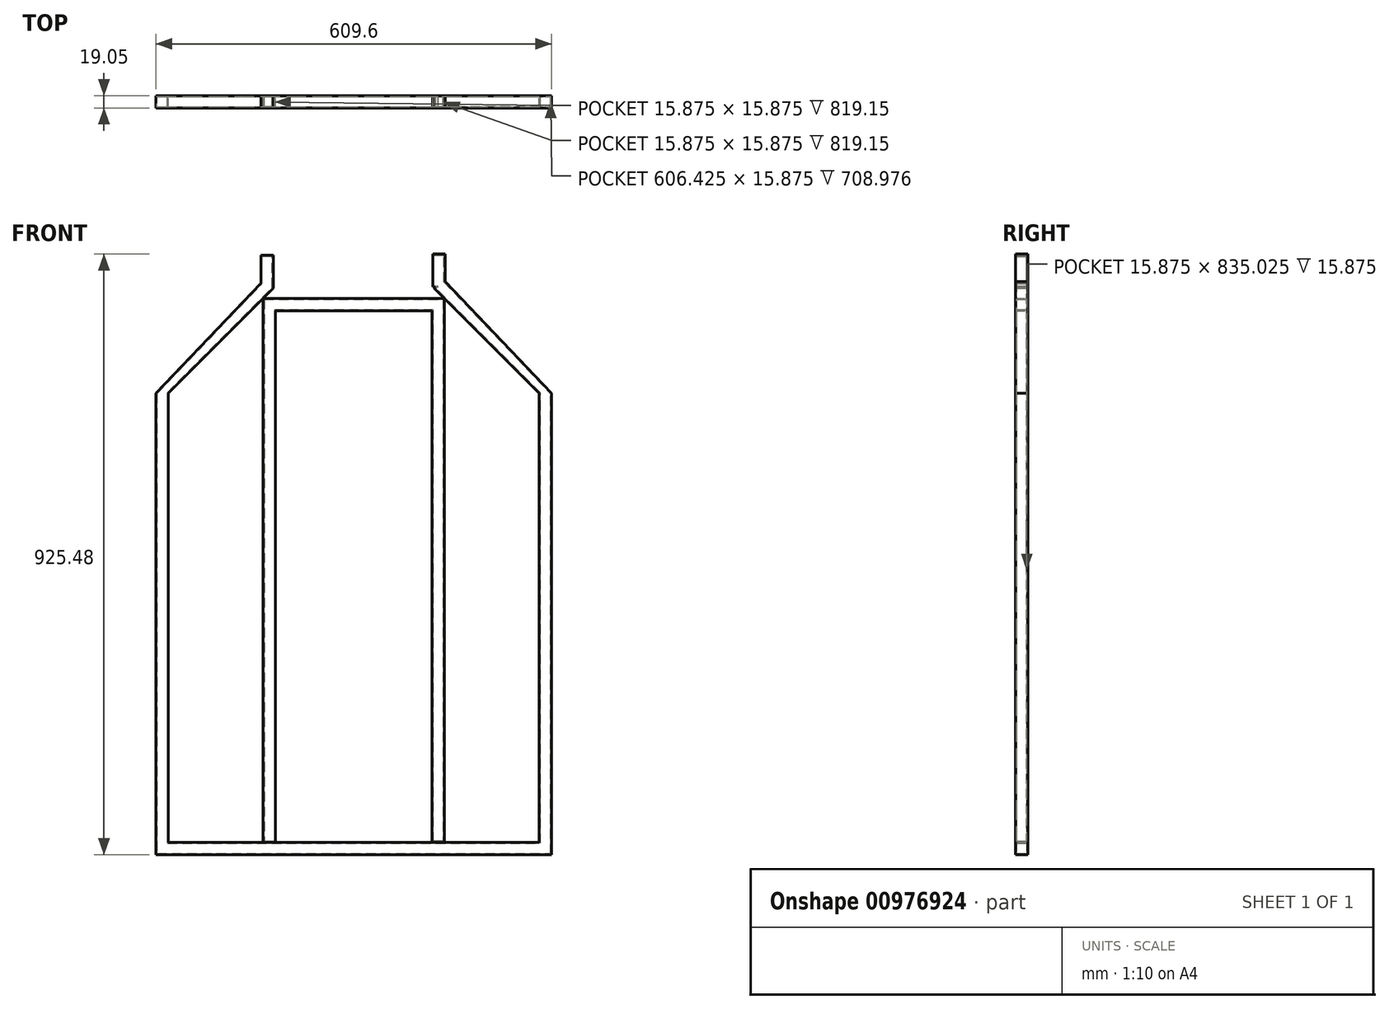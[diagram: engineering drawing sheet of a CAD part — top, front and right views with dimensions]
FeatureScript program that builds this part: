
annotation { "Feature Type Name" : "Feature", "Feature Type Description" : "" }
export const myFeature = defineFeature(function(context is Context, id is Id, definition is map)
    precondition{}
    {
        {
            var Q0;
            Q0=qCreatedBy(makeId("Front.planeOp"),FACE);
            var sketch = newSketch(context, id + "F0", { "sketchPlane" : qUnion([Q0])});
            skLineSegment(sketch, "E0.bottom", {"start": v(-363.02, 291.08) * mm, "end": v(-343.97, 291.08) * mm});
            skLineSegment(sketch, "E0.top", {"start": v(-363.02, -420.12) * mm, "end": v(-343.97, -420.12) * mm});
            skLineSegment(sketch, "E0.left", {"start": v(-363.02, 291.08) * mm, "end": v(-363.02, -420.12) * mm});
            skLineSegment(sketch, "E0.right", {"start": v(-343.97, 291.08) * mm, "end": v(-343.97, -420.12) * mm});
            skLineSegment(sketch, "E1.bottom", {"start": v(-343.97, -420.12) * mm, "end": v(246.58, -420.12) * mm});
            skLineSegment(sketch, "E1.top", {"start": v(-343.97, -401.07) * mm, "end": v(246.58, -401.07) * mm});
            skLineSegment(sketch, "E1.left", {"start": v(-343.97, -420.12) * mm, "end": v(-343.97, -401.07) * mm});
            skLineSegment(sketch, "E1.right", {"start": v(246.58, -420.12) * mm, "end": v(246.58, -401.07) * mm});
            skLineSegment(sketch, "E2.bottom", {"start": v(246.58, -401.07) * mm, "end": v(227.53, -401.07) * mm});
            skLineSegment(sketch, "E2.top", {"start": v(246.58, 291.08) * mm, "end": v(227.53, 291.08) * mm});
            skLineSegment(sketch, "E2.left", {"start": v(246.58, -401.07) * mm, "end": v(246.58, 291.08) * mm});
            skLineSegment(sketch, "E2.right", {"start": v(227.53, -401.07) * mm, "end": v(227.53, 291.08) * mm});
            skLineSegment(sketch, "E3", {"start": v(-363.02, 291.08) * mm, "end": v(-196.1, 465.88) * mm});
            skLineSegment(sketch, "E4", {"start": v(-196.1, 465.88) * mm, "end": v(-182.32, 452.72) * mm});
            skLineSegment(sketch, "E5", {"start": v(-343.97, 291.08) * mm, "end": v(-182.32, 452.72) * mm});
            skLineSegment(sketch, "E6", {"start": v(227.53, 291.08) * mm, "end": v(65.89, 452.72) * mm});
            skLineSegment(sketch, "E7", {"start": v(65.89, 452.72) * mm, "end": v(79.66, 465.88) * mm});
            skLineSegment(sketch, "E8", {"start": v(79.66, 465.88) * mm, "end": v(246.58, 291.08) * mm});
            skLineSegment(sketch, "E9.bottom", {"start": v(-182.32, 452.72) * mm, "end": v(-201.37, 452.72) * mm});
            skLineSegment(sketch, "E9.top", {"start": v(-182.32, 503.52) * mm, "end": v(-201.37, 503.52) * mm});
            skLineSegment(sketch, "E9.left", {"start": v(-182.32, 452.72) * mm, "end": v(-182.32, 503.52) * mm});
            skLineSegment(sketch, "E9.right", {"start": v(-201.37, 452.72) * mm, "end": v(-201.37, 503.52) * mm});
            skLineSegment(sketch, "E10.bottom", {"start": v(63.49, 454.56) * mm, "end": v(82.54, 454.56) * mm});
            skLineSegment(sketch, "E10.top", {"start": v(63.49, 505.36) * mm, "end": v(82.54, 505.36) * mm});
            skLineSegment(sketch, "E10.left", {"start": v(63.49, 454.56) * mm, "end": v(63.49, 505.36) * mm});
            skLineSegment(sketch, "E10.right", {"start": v(82.54, 454.56) * mm, "end": v(82.54, 505.36) * mm});
            skPoint(sketch, "E11", {"position": v(81.48, -401.07) * mm});
            skPoint(sketch, "E12", {"position": v(-197.92, -401.07) * mm});
            skSolve(sketch);
        }
        {
            var Q0;
            Q0 = qSketchRegion(id + "F0", true);
            extrude(context, id + "F1", {"entities" : qUnion([Q0]), "depth" : 19.05 * mm, "offsetDistance" : 25.4 * mm});
        }
        {
            var Q0;
            Q0=qCreatedBy(makeId("Front.planeOp"),FACE);
            var sketch = newSketch(context, id + "F2", { "sketchPlane" : qUnion([Q0])});
            skLineSegment(sketch, "E13.bottom", {"start": v(-197.92, 437.13) * mm, "end": v(81.48, 437.13) * mm});
            skLineSegment(sketch, "E13.top", {"start": v(-197.92, 418.08) * mm, "end": v(81.48, 418.08) * mm});
            skLineSegment(sketch, "E13.left", {"start": v(-197.92, 437.13) * mm, "end": v(-197.92, 418.08) * mm});
            skLineSegment(sketch, "E13.right", {"start": v(81.48, 437.13) * mm, "end": v(81.48, 418.08) * mm});
            skLineSegment(sketch, "E14.bottom", {"start": v(-197.92, 418.08) * mm, "end": v(-178.87, 418.08) * mm});
            skLineSegment(sketch, "E14.top", {"start": v(-197.92, -401.07) * mm, "end": v(-178.87, -401.07) * mm});
            skLineSegment(sketch, "E14.left", {"start": v(-197.92, 418.08) * mm, "end": v(-197.92, -401.07) * mm});
            skLineSegment(sketch, "E14.right", {"start": v(-178.87, 418.08) * mm, "end": v(-178.87, -401.07) * mm});
            skLineSegment(sketch, "E15.bottom", {"start": v(81.48, 418.08) * mm, "end": v(62.43, 418.08) * mm});
            skLineSegment(sketch, "E15.top", {"start": v(81.48, -401.07) * mm, "end": v(62.43, -401.07) * mm});
            skLineSegment(sketch, "E15.left", {"start": v(81.48, 418.08) * mm, "end": v(81.48, -401.07) * mm});
            skLineSegment(sketch, "E15.right", {"start": v(62.43, 418.08) * mm, "end": v(62.43, -401.07) * mm});
            skSolve(sketch);
        }
        {
            var Q0;
            Q0 = qSketchRegion(id + "F2", true);
            extrude(context, id + "F3", {"entities" : qUnion([Q0]), "depth" : 19.05 * mm, "offsetDistance" : 25.4 * mm});
        }
        {
            var Q0;
            Q0=makeQuery(id+"F1.opExtrude","CAP_FACE",FACE,{"disambiguationData":[OSD([sQuery(id+"F0.wireOp",EDGE,"E0.top"),sQuery(id+"F0.wireOp",EDGE,"E0.left"),sQuery(id+"F0.wireOp",EDGE,"E0.right"),sQuery(id+"F0.wireOp",EDGE,"E1.bottom"),sQuery(id+"F0.wireOp",EDGE,"E1.top"),sQuery(id+"F0.wireOp",EDGE,"E1.right"),sQuery(id+"F0.wireOp",EDGE,"E2.left"),sQuery(id+"F0.wireOp",EDGE,"E2.right"),sQuery(id+"F0.wireOp",EDGE,"E3"),sQuery(id+"F0.wireOp",EDGE,"E5"),sQuery(id+"F0.wireOp",EDGE,"E6"),sQuery(id+"F0.wireOp",EDGE,"E7"),sQuery(id+"F0.wireOp",EDGE,"E8"),sQuery(id+"F0.wireOp",EDGE,"E9.top"),sQuery(id+"F0.wireOp",EDGE,"E9.left"),sQuery(id+"F0.wireOp",EDGE,"E9.right"),sQuery(id+"F0.wireOp",EDGE,"E10.bottom"),sQuery(id+"F0.wireOp",EDGE,"E10.top"),sQuery(id+"F0.wireOp",EDGE,"E10.left"),sQuery(id+"F0.wireOp",EDGE,"E10.right")])],"isStart":true});
            var Q1;
            Q1=makeQuery(id+"F3.opExtrude","CAP_FACE",FACE,{"disambiguationData":[OSD([sQuery(id+"F2.wireOp",EDGE,"E13.bottom"),sQuery(id+"F2.wireOp",EDGE,"E13.top"),sQuery(id+"F2.wireOp",EDGE,"E13.left"),sQuery(id+"F2.wireOp",EDGE,"E13.right"),sQuery(id+"F2.wireOp",EDGE,"E14.top"),sQuery(id+"F2.wireOp",EDGE,"E14.left"),sQuery(id+"F2.wireOp",EDGE,"E14.right"),sQuery(id+"F2.wireOp",EDGE,"E15.top"),sQuery(id+"F2.wireOp",EDGE,"E15.left"),sQuery(id+"F2.wireOp",EDGE,"E15.right")])],"isStart":true});
            var Q2;
            Q2=makeQuery(id+"F1.opExtrude","SWEPT_BODY",BODY,{"disambiguationData":[OSD([sQuery(id+"F0.wireOp",EDGE,"E0.top"),sQuery(id+"F0.wireOp",EDGE,"E0.left"),sQuery(id+"F0.wireOp",EDGE,"E0.right"),sQuery(id+"F0.wireOp",EDGE,"E1.bottom"),sQuery(id+"F0.wireOp",EDGE,"E1.top"),sQuery(id+"F0.wireOp",EDGE,"E1.right"),sQuery(id+"F0.wireOp",EDGE,"E2.left"),sQuery(id+"F0.wireOp",EDGE,"E2.right"),sQuery(id+"F0.wireOp",EDGE,"E3"),sQuery(id+"F0.wireOp",EDGE,"E5"),sQuery(id+"F0.wireOp",EDGE,"E6"),sQuery(id+"F0.wireOp",EDGE,"E7"),sQuery(id+"F0.wireOp",EDGE,"E8"),sQuery(id+"F0.wireOp",EDGE,"E9.top"),sQuery(id+"F0.wireOp",EDGE,"E9.left"),sQuery(id+"F0.wireOp",EDGE,"E9.right"),sQuery(id+"F0.wireOp",EDGE,"E10.bottom"),sQuery(id+"F0.wireOp",EDGE,"E10.top"),sQuery(id+"F0.wireOp",EDGE,"E10.left"),sQuery(id+"F0.wireOp",EDGE,"E10.right")])]});
            var Q3;
            Q3=makeQuery(id+"F3.opExtrude","SWEPT_BODY",BODY,{"disambiguationData":[OSD([sQuery(id+"F2.wireOp",EDGE,"E13.bottom"),sQuery(id+"F2.wireOp",EDGE,"E13.top"),sQuery(id+"F2.wireOp",EDGE,"E13.left"),sQuery(id+"F2.wireOp",EDGE,"E13.right"),sQuery(id+"F2.wireOp",EDGE,"E14.top"),sQuery(id+"F2.wireOp",EDGE,"E14.left"),sQuery(id+"F2.wireOp",EDGE,"E14.right"),sQuery(id+"F2.wireOp",EDGE,"E15.top"),sQuery(id+"F2.wireOp",EDGE,"E15.left"),sQuery(id+"F2.wireOp",EDGE,"E15.right")])]});
            shell(context, id + "F4", {"isHollow" : true, "entities" : qUnion([Q0, Q1]), "parts" : qUnion([Q2, Q3]), "thickness" : 1.59 * mm});
        }
    });
